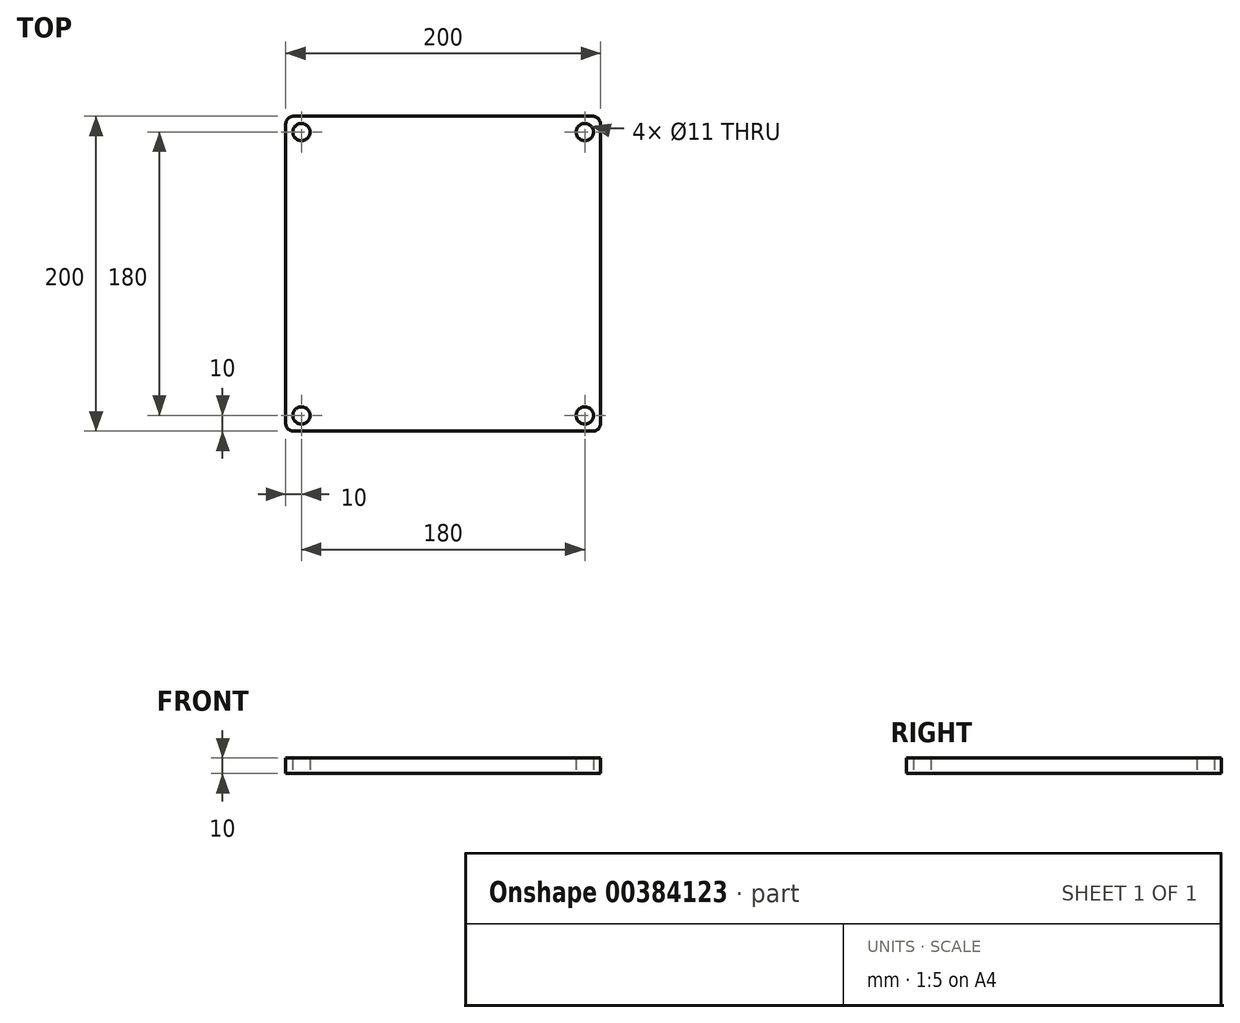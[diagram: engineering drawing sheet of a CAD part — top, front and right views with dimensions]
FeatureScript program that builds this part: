
annotation { "Feature Type Name" : "Feature", "Feature Type Description" : "" }
export const myFeature = defineFeature(function(context is Context, id is Id, definition is map)
    precondition{}
    {
        {
            var Q0;
            Q0=qCreatedBy(makeId("Top.planeOp"),FACE);
            var sketch = newSketch(context, id + "F0", { "sketchPlane" : qUnion([Q0])});
            skLineSegment(sketch, "E0.bottom", {"start": v(95, 100) * mm, "end": v(-95, 100) * mm});
            skLineSegment(sketch, "E0.top", {"start": v(95, -100) * mm, "end": v(-95, -100) * mm});
            skLineSegment(sketch, "E0.left", {"start": v(100, 95) * mm, "end": v(100, -95) * mm});
            skLineSegment(sketch, "E0.right", {"start": v(-100, 95) * mm, "end": v(-100, -95) * mm});
            skPoint(sketch, "E0.middle", {"position": v(0, 0) * mm});
            skPoint(sketch, "E1.visualSharp", {"position": v(100, 100) * mm});
            skArc(sketch, "E1.filletArc", {"start": v(100, 95) * mm, "mid": v(98.54, 98.54) * mm, "end": v(95, 100) * mm});
            skPoint(sketch, "E2.visualSharp", {"position": v(-100, 100) * mm});
            skArc(sketch, "E2.filletArc", {"start": v(-95, 100) * mm, "mid": v(-98.54, 98.54) * mm, "end": v(-100, 95) * mm});
            skPoint(sketch, "E3.visualSharp", {"position": v(-100, -100) * mm});
            skArc(sketch, "E3.filletArc", {"start": v(-100, -95) * mm, "mid": v(-98.54, -98.54) * mm, "end": v(-95, -100) * mm});
            skPoint(sketch, "E4.visualSharp", {"position": v(100, -100) * mm});
            skArc(sketch, "E4.filletArc", {"start": v(95, -100) * mm, "mid": v(98.54, -98.54) * mm, "end": v(100, -95) * mm});
            skCircle(sketch, "E5", {"center": v(-90, 90) * mm, "radius": 5.5 * mm});
            skCircle(sketch, "E6.0.1.0", {"center": v(-90, -90) * mm, "radius": 5.5 * mm});
            skCircle(sketch, "E6.1.0.0", {"center": v(90, 90) * mm, "radius": 5.5 * mm});
            skCircle(sketch, "E6.1.1.0", {"center": v(90, -90) * mm, "radius": 5.5 * mm});
            skLineSegment(sketch, "E6.direction1", {"start": v(-90, 90) * mm, "end": v(90, 90) * mm, "construction": true});
            skLineSegment(sketch, "E6.direction2", {"start": v(-90, 90) * mm, "end": v(-90, -90) * mm, "construction": true});
            skSolve(sketch);
        }
        {
            var Q0;
            Q0=makeQuery(id+"F0.imprint","IMPRINT",FACE,{"disambiguationData":[TD([[makeQuery(id+"F0.imprint","IMPRINT",EDGE,{"derivedFrom":sQuery(id+"F0.wireOp",EDGE,"E0.bottom")}),1.0]])]});
            extrude(context, id + "F1", {"entities" : qUnion([Q0]), "depth" : 10 * mm});
        }
    });
